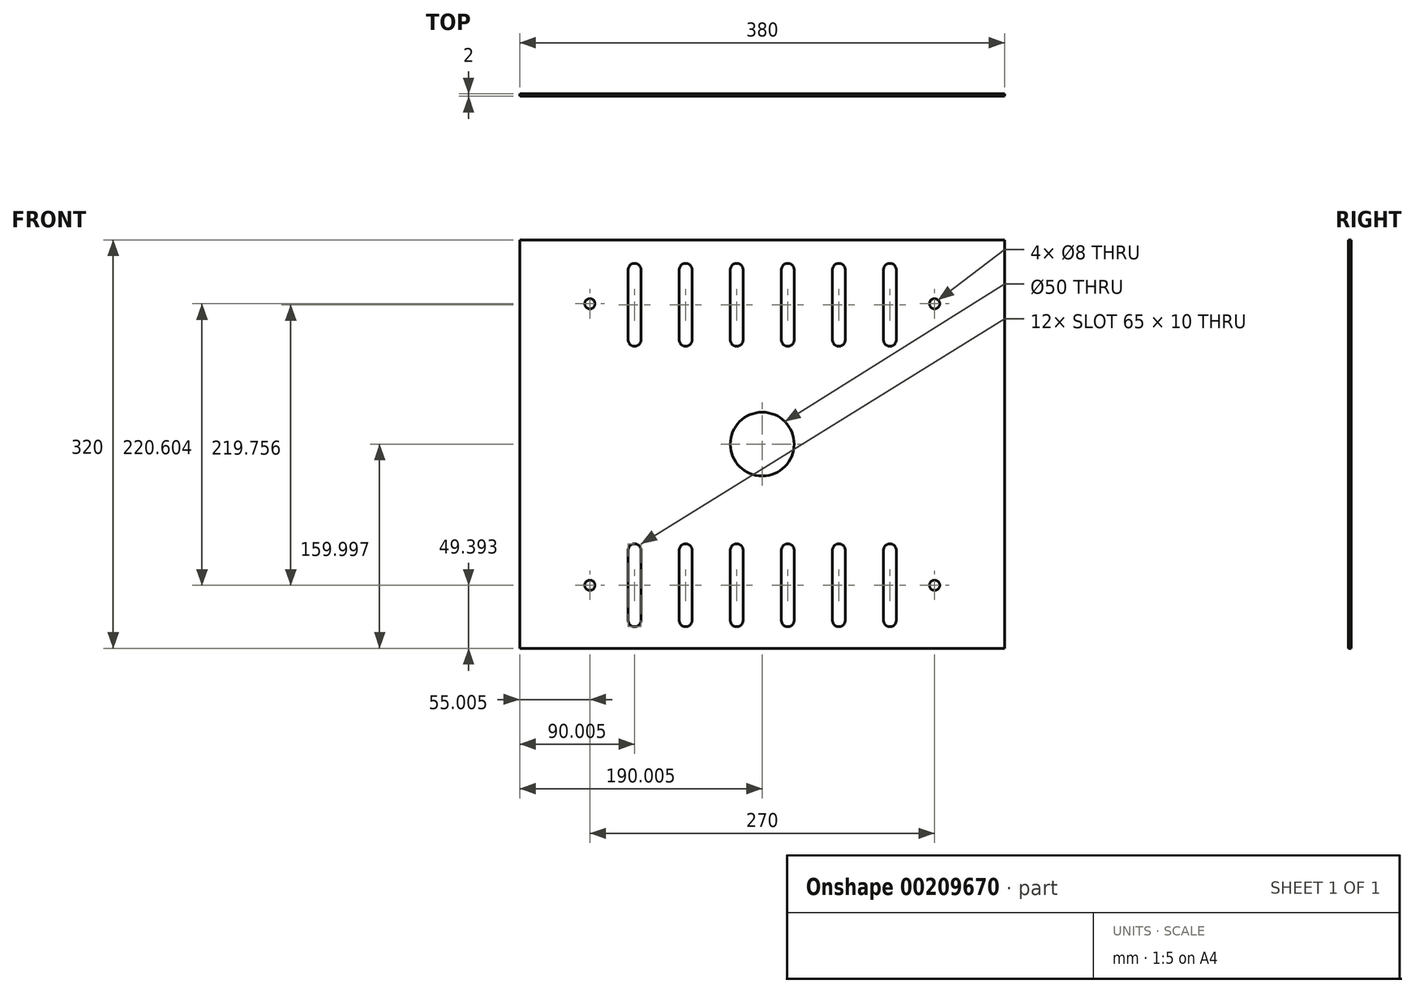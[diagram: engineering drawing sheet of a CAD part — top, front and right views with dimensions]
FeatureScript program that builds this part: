
annotation { "Feature Type Name" : "Feature", "Feature Type Description" : "" }
export const myFeature = defineFeature(function(context is Context, id is Id, definition is map)
    precondition{}
    {
        {
            var Q0;
            Q0=qCreatedBy(makeId("Front.planeOp"),FACE);
            var sketch = newSketch(context, id + "F0", { "sketchPlane" : qUnion([Q0])});
            skLineSegment(sketch, "E0.bottom", {"start": v(-8022.28, 365.36) * mm, "end": v(-7642.28, 365.36) * mm});
            skLineSegment(sketch, "E0.top", {"start": v(-8022.28, 45.36) * mm, "end": v(-7642.28, 45.36) * mm});
            skLineSegment(sketch, "E0.left", {"start": v(-8022.28, 365.36) * mm, "end": v(-8022.28, 45.36) * mm});
            skLineSegment(sketch, "E0.right", {"start": v(-7642.28, 365.36) * mm, "end": v(-7642.28, 45.36) * mm});
            skPoint(sketch, "E1", {"position": v(-7967.28, 315.36) * mm});
            skPoint(sketch, "E2", {"position": v(-7697.28, 315.36) * mm});
            skPoint(sketch, "E3", {"position": v(-7967.28, 94.75) * mm});
            skPoint(sketch, "E4", {"position": v(-7697.28, 94.75) * mm});
            skPoint(sketch, "E5", {"position": v(-7832.28, 365.36) * mm});
            skPoint(sketch, "E6", {"position": v(-8022.28, 205.36) * mm});
            skPoint(sketch, "E7", {"position": v(-7832.28, 205.36) * mm});
            skCircle(sketch, "E8", {"center": v(-7832.28, 205.36) * mm, "radius": 25 * mm});
            skCircle(sketch, "E9", {"center": v(-7967.28, 315.36) * mm, "radius": 4 * mm});
            skCircle(sketch, "E10", {"center": v(-7967.28, 94.75) * mm, "radius": 4 * mm});
            skCircle(sketch, "E11", {"center": v(-7697.28, 315.36) * mm, "radius": 4 * mm});
            skCircle(sketch, "E12", {"center": v(-7697.28, 94.75) * mm, "radius": 4 * mm});
            skPoint(sketch, "E13", {"position": v(-7932.28, 94.75) * mm});
            skLineSegment(sketch, "E14.bottom", {"start": v(-7932.28, 127.25) * mm, "end": v(-7932.28, 127.25) * mm});
            skLineSegment(sketch, "E14.top", {"start": v(-7932.28, 62.25) * mm, "end": v(-7932.28, 62.25) * mm});
            skLineSegment(sketch, "E14.left", {"start": v(-7927.28, 122.25) * mm, "end": v(-7927.28, 67.25) * mm});
            skLineSegment(sketch, "E14.right", {"start": v(-7937.28, 122.25) * mm, "end": v(-7937.28, 67.25) * mm});
            skPoint(sketch, "E15.visualSharp", {"position": v(-7937.28, 127.25) * mm});
            skArc(sketch, "E15.filletArc", {"start": v(-7932.28, 127.25) * mm, "mid": v(-7935.81, 125.79) * mm, "end": v(-7937.28, 122.25) * mm});
            skPoint(sketch, "E16.visualSharp", {"position": v(-7927.28, 127.25) * mm});
            skArc(sketch, "E16.filletArc", {"start": v(-7927.28, 122.25) * mm, "mid": v(-7928.74, 125.79) * mm, "end": v(-7932.28, 127.25) * mm});
            skPoint(sketch, "E17.visualSharp", {"position": v(-7927.28, 62.25) * mm});
            skArc(sketch, "E17.filletArc", {"start": v(-7932.28, 62.25) * mm, "mid": v(-7928.74, 63.72) * mm, "end": v(-7927.28, 67.25) * mm});
            skPoint(sketch, "E18.visualSharp", {"position": v(-7937.28, 62.25) * mm});
            skArc(sketch, "E18.filletArc", {"start": v(-7937.28, 67.25) * mm, "mid": v(-7935.81, 63.72) * mm, "end": v(-7932.28, 62.25) * mm});
            skPoint(sketch, "E19", {"position": v(-7892.28, 94.75) * mm});
            skLineSegment(sketch, "E20.bottom", {"start": v(-7892.28, 127.25) * mm, "end": v(-7892.28, 127.25) * mm});
            skLineSegment(sketch, "E20.top", {"start": v(-7892.28, 62.25) * mm, "end": v(-7892.28, 62.25) * mm});
            skLineSegment(sketch, "E20.left", {"start": v(-7887.28, 122.25) * mm, "end": v(-7887.28, 67.25) * mm});
            skLineSegment(sketch, "E20.right", {"start": v(-7897.28, 122.25) * mm, "end": v(-7897.28, 67.25) * mm});
            skPoint(sketch, "E21.visualSharp", {"position": v(-7897.28, 127.25) * mm});
            skArc(sketch, "E21.filletArc", {"start": v(-7892.28, 127.25) * mm, "mid": v(-7895.81, 125.79) * mm, "end": v(-7897.28, 122.25) * mm});
            skPoint(sketch, "E22.visualSharp", {"position": v(-7887.28, 127.25) * mm});
            skArc(sketch, "E22.filletArc", {"start": v(-7887.28, 122.25) * mm, "mid": v(-7888.74, 125.79) * mm, "end": v(-7892.28, 127.25) * mm});
            skPoint(sketch, "E23.visualSharp", {"position": v(-7887.28, 62.25) * mm});
            skArc(sketch, "E23.filletArc", {"start": v(-7892.28, 62.25) * mm, "mid": v(-7888.74, 63.72) * mm, "end": v(-7887.28, 67.25) * mm});
            skPoint(sketch, "E24.visualSharp", {"position": v(-7897.28, 62.25) * mm});
            skArc(sketch, "E24.filletArc", {"start": v(-7897.28, 67.25) * mm, "mid": v(-7895.81, 63.72) * mm, "end": v(-7892.28, 62.25) * mm});
            skPoint(sketch, "E25", {"position": v(-7852.28, 94.75) * mm});
            skLineSegment(sketch, "E26.bottom", {"start": v(-7852.28, 127.25) * mm, "end": v(-7852.28, 127.25) * mm});
            skLineSegment(sketch, "E26.top", {"start": v(-7852.28, 62.25) * mm, "end": v(-7852.28, 62.25) * mm});
            skLineSegment(sketch, "E26.left", {"start": v(-7847.28, 122.25) * mm, "end": v(-7847.28, 67.25) * mm});
            skLineSegment(sketch, "E26.right", {"start": v(-7857.28, 122.25) * mm, "end": v(-7857.28, 67.25) * mm});
            skPoint(sketch, "E27.visualSharp", {"position": v(-7857.28, 127.25) * mm});
            skArc(sketch, "E27.filletArc", {"start": v(-7852.28, 127.25) * mm, "mid": v(-7855.81, 125.79) * mm, "end": v(-7857.28, 122.25) * mm});
            skPoint(sketch, "E28.visualSharp", {"position": v(-7847.28, 127.25) * mm});
            skArc(sketch, "E28.filletArc", {"start": v(-7847.28, 122.25) * mm, "mid": v(-7848.74, 125.79) * mm, "end": v(-7852.28, 127.25) * mm});
            skPoint(sketch, "E29.visualSharp", {"position": v(-7847.28, 62.25) * mm});
            skArc(sketch, "E29.filletArc", {"start": v(-7852.28, 62.25) * mm, "mid": v(-7848.74, 63.72) * mm, "end": v(-7847.28, 67.25) * mm});
            skPoint(sketch, "E30.visualSharp", {"position": v(-7857.28, 62.25) * mm});
            skArc(sketch, "E30.filletArc", {"start": v(-7857.28, 67.25) * mm, "mid": v(-7855.81, 63.72) * mm, "end": v(-7852.28, 62.25) * mm});
            skPoint(sketch, "E31", {"position": v(-7812.28, 94.75) * mm});
            skLineSegment(sketch, "E32.bottom", {"start": v(-7812.28, 127.25) * mm, "end": v(-7812.28, 127.25) * mm});
            skLineSegment(sketch, "E32.top", {"start": v(-7812.28, 62.25) * mm, "end": v(-7812.28, 62.25) * mm});
            skLineSegment(sketch, "E32.left", {"start": v(-7807.28, 122.25) * mm, "end": v(-7807.28, 67.25) * mm});
            skLineSegment(sketch, "E32.right", {"start": v(-7817.28, 122.25) * mm, "end": v(-7817.28, 67.25) * mm});
            skPoint(sketch, "E33.visualSharp", {"position": v(-7817.28, 127.25) * mm});
            skArc(sketch, "E33.filletArc", {"start": v(-7812.28, 127.25) * mm, "mid": v(-7815.81, 125.79) * mm, "end": v(-7817.28, 122.25) * mm});
            skPoint(sketch, "E34.visualSharp", {"position": v(-7807.28, 127.25) * mm});
            skArc(sketch, "E34.filletArc", {"start": v(-7807.28, 122.25) * mm, "mid": v(-7808.74, 125.79) * mm, "end": v(-7812.28, 127.25) * mm});
            skPoint(sketch, "E35.visualSharp", {"position": v(-7807.28, 62.25) * mm});
            skArc(sketch, "E35.filletArc", {"start": v(-7812.28, 62.25) * mm, "mid": v(-7808.74, 63.72) * mm, "end": v(-7807.28, 67.25) * mm});
            skPoint(sketch, "E36.visualSharp", {"position": v(-7817.28, 62.25) * mm});
            skArc(sketch, "E36.filletArc", {"start": v(-7817.28, 67.25) * mm, "mid": v(-7815.81, 63.72) * mm, "end": v(-7812.28, 62.25) * mm});
            skPoint(sketch, "E37", {"position": v(-7772.28, 94.75) * mm});
            skLineSegment(sketch, "E38.bottom", {"start": v(-7772.28, 127.25) * mm, "end": v(-7772.28, 127.25) * mm});
            skLineSegment(sketch, "E38.top", {"start": v(-7772.28, 62.25) * mm, "end": v(-7772.28, 62.25) * mm});
            skLineSegment(sketch, "E38.left", {"start": v(-7767.28, 122.25) * mm, "end": v(-7767.28, 67.25) * mm});
            skLineSegment(sketch, "E38.right", {"start": v(-7777.28, 122.25) * mm, "end": v(-7777.28, 67.25) * mm});
            skPoint(sketch, "E39.visualSharp", {"position": v(-7777.28, 127.25) * mm});
            skArc(sketch, "E39.filletArc", {"start": v(-7772.28, 127.25) * mm, "mid": v(-7775.81, 125.79) * mm, "end": v(-7777.28, 122.25) * mm});
            skPoint(sketch, "E40.visualSharp", {"position": v(-7767.28, 127.25) * mm});
            skArc(sketch, "E40.filletArc", {"start": v(-7767.28, 122.25) * mm, "mid": v(-7768.74, 125.79) * mm, "end": v(-7772.28, 127.25) * mm});
            skPoint(sketch, "E41.visualSharp", {"position": v(-7767.28, 62.25) * mm});
            skArc(sketch, "E41.filletArc", {"start": v(-7772.28, 62.25) * mm, "mid": v(-7768.74, 63.72) * mm, "end": v(-7767.28, 67.25) * mm});
            skPoint(sketch, "E42.visualSharp", {"position": v(-7777.28, 62.25) * mm});
            skArc(sketch, "E42.filletArc", {"start": v(-7777.28, 67.25) * mm, "mid": v(-7775.81, 63.72) * mm, "end": v(-7772.28, 62.25) * mm});
            skPoint(sketch, "E43", {"position": v(-7732.28, 94.75) * mm});
            skLineSegment(sketch, "E44.bottom", {"start": v(-7732.28, 127.25) * mm, "end": v(-7732.28, 127.25) * mm});
            skLineSegment(sketch, "E44.top", {"start": v(-7732.28, 62.25) * mm, "end": v(-7732.28, 62.25) * mm});
            skLineSegment(sketch, "E44.left", {"start": v(-7727.28, 122.25) * mm, "end": v(-7727.28, 67.25) * mm});
            skLineSegment(sketch, "E44.right", {"start": v(-7737.28, 122.25) * mm, "end": v(-7737.28, 67.25) * mm});
            skPoint(sketch, "E45.visualSharp", {"position": v(-7737.28, 127.25) * mm});
            skArc(sketch, "E45.filletArc", {"start": v(-7732.28, 127.25) * mm, "mid": v(-7735.81, 125.79) * mm, "end": v(-7737.28, 122.25) * mm});
            skPoint(sketch, "E46.visualSharp", {"position": v(-7727.28, 127.25) * mm});
            skArc(sketch, "E46.filletArc", {"start": v(-7727.28, 122.25) * mm, "mid": v(-7728.74, 125.79) * mm, "end": v(-7732.28, 127.25) * mm});
            skPoint(sketch, "E47.visualSharp", {"position": v(-7727.28, 62.25) * mm});
            skArc(sketch, "E47.filletArc", {"start": v(-7732.28, 62.25) * mm, "mid": v(-7728.74, 63.72) * mm, "end": v(-7727.28, 67.25) * mm});
            skPoint(sketch, "E48.visualSharp", {"position": v(-7737.28, 62.25) * mm});
            skArc(sketch, "E48.filletArc", {"start": v(-7737.28, 67.25) * mm, "mid": v(-7735.81, 63.72) * mm, "end": v(-7732.28, 62.25) * mm});
            skPoint(sketch, "E49", {"position": v(-7932.28, 314.5) * mm});
            skLineSegment(sketch, "E50.bottom", {"start": v(-7932.28, 347) * mm, "end": v(-7932.28, 347) * mm});
            skLineSegment(sketch, "E50.top", {"start": v(-7932.28, 282) * mm, "end": v(-7932.28, 282) * mm});
            skLineSegment(sketch, "E50.left", {"start": v(-7927.28, 342) * mm, "end": v(-7927.28, 287) * mm});
            skLineSegment(sketch, "E50.right", {"start": v(-7937.28, 342) * mm, "end": v(-7937.28, 287) * mm});
            skPoint(sketch, "E51.visualSharp", {"position": v(-7937.28, 347) * mm});
            skArc(sketch, "E51.filletArc", {"start": v(-7932.28, 347) * mm, "mid": v(-7935.81, 345.54) * mm, "end": v(-7937.28, 342) * mm});
            skPoint(sketch, "E52.visualSharp", {"position": v(-7927.28, 347) * mm});
            skArc(sketch, "E52.filletArc", {"start": v(-7927.28, 342) * mm, "mid": v(-7928.74, 345.54) * mm, "end": v(-7932.28, 347) * mm});
            skPoint(sketch, "E53.visualSharp", {"position": v(-7927.28, 282) * mm});
            skArc(sketch, "E53.filletArc", {"start": v(-7932.28, 282) * mm, "mid": v(-7928.74, 283.47) * mm, "end": v(-7927.28, 287) * mm});
            skPoint(sketch, "E54.visualSharp", {"position": v(-7937.28, 282) * mm});
            skArc(sketch, "E54.filletArc", {"start": v(-7937.28, 287) * mm, "mid": v(-7935.81, 283.47) * mm, "end": v(-7932.28, 282) * mm});
            skPoint(sketch, "E55", {"position": v(-7892.28, 314.5) * mm});
            skLineSegment(sketch, "E56.bottom", {"start": v(-7892.28, 347) * mm, "end": v(-7892.28, 347) * mm});
            skLineSegment(sketch, "E56.top", {"start": v(-7892.28, 282) * mm, "end": v(-7892.28, 282) * mm});
            skLineSegment(sketch, "E56.left", {"start": v(-7887.28, 342) * mm, "end": v(-7887.28, 287) * mm});
            skLineSegment(sketch, "E56.right", {"start": v(-7897.28, 342) * mm, "end": v(-7897.28, 287) * mm});
            skPoint(sketch, "E57.visualSharp", {"position": v(-7897.28, 347) * mm});
            skArc(sketch, "E57.filletArc", {"start": v(-7892.28, 347) * mm, "mid": v(-7895.81, 345.54) * mm, "end": v(-7897.28, 342) * mm});
            skPoint(sketch, "E58.visualSharp", {"position": v(-7887.28, 347) * mm});
            skArc(sketch, "E58.filletArc", {"start": v(-7887.28, 342) * mm, "mid": v(-7888.74, 345.54) * mm, "end": v(-7892.28, 347) * mm});
            skPoint(sketch, "E59.visualSharp", {"position": v(-7887.28, 282) * mm});
            skArc(sketch, "E59.filletArc", {"start": v(-7892.28, 282) * mm, "mid": v(-7888.74, 283.47) * mm, "end": v(-7887.28, 287) * mm});
            skPoint(sketch, "E60.visualSharp", {"position": v(-7897.28, 282) * mm});
            skArc(sketch, "E60.filletArc", {"start": v(-7897.28, 287) * mm, "mid": v(-7895.81, 283.47) * mm, "end": v(-7892.28, 282) * mm});
            skPoint(sketch, "E61", {"position": v(-7852.28, 314.5) * mm});
            skLineSegment(sketch, "E62.bottom", {"start": v(-7852.28, 347) * mm, "end": v(-7852.28, 347) * mm});
            skLineSegment(sketch, "E62.top", {"start": v(-7852.28, 282) * mm, "end": v(-7852.28, 282) * mm});
            skLineSegment(sketch, "E62.left", {"start": v(-7847.28, 342) * mm, "end": v(-7847.28, 287) * mm});
            skLineSegment(sketch, "E62.right", {"start": v(-7857.28, 342) * mm, "end": v(-7857.28, 287) * mm});
            skPoint(sketch, "E63.visualSharp", {"position": v(-7857.28, 347) * mm});
            skArc(sketch, "E63.filletArc", {"start": v(-7852.28, 347) * mm, "mid": v(-7855.81, 345.54) * mm, "end": v(-7857.28, 342) * mm});
            skPoint(sketch, "E64.visualSharp", {"position": v(-7847.28, 347) * mm});
            skArc(sketch, "E64.filletArc", {"start": v(-7847.28, 342) * mm, "mid": v(-7848.74, 345.54) * mm, "end": v(-7852.28, 347) * mm});
            skPoint(sketch, "E65.visualSharp", {"position": v(-7847.28, 282) * mm});
            skArc(sketch, "E65.filletArc", {"start": v(-7852.28, 282) * mm, "mid": v(-7848.74, 283.47) * mm, "end": v(-7847.28, 287) * mm});
            skPoint(sketch, "E66.visualSharp", {"position": v(-7857.28, 282) * mm});
            skArc(sketch, "E66.filletArc", {"start": v(-7857.28, 287) * mm, "mid": v(-7855.81, 283.47) * mm, "end": v(-7852.28, 282) * mm});
            skPoint(sketch, "E67", {"position": v(-7812.28, 314.5) * mm});
            skLineSegment(sketch, "E68.bottom", {"start": v(-7812.28, 347) * mm, "end": v(-7812.28, 347) * mm});
            skLineSegment(sketch, "E68.top", {"start": v(-7812.28, 282) * mm, "end": v(-7812.28, 282) * mm});
            skLineSegment(sketch, "E68.left", {"start": v(-7807.28, 342) * mm, "end": v(-7807.28, 287) * mm});
            skLineSegment(sketch, "E68.right", {"start": v(-7817.28, 342) * mm, "end": v(-7817.28, 287) * mm});
            skPoint(sketch, "E69.visualSharp", {"position": v(-7817.28, 347) * mm});
            skArc(sketch, "E69.filletArc", {"start": v(-7812.28, 347) * mm, "mid": v(-7815.81, 345.54) * mm, "end": v(-7817.28, 342) * mm});
            skPoint(sketch, "E70.visualSharp", {"position": v(-7807.28, 347) * mm});
            skArc(sketch, "E70.filletArc", {"start": v(-7807.28, 342) * mm, "mid": v(-7808.74, 345.54) * mm, "end": v(-7812.28, 347) * mm});
            skPoint(sketch, "E71.visualSharp", {"position": v(-7807.28, 282) * mm});
            skArc(sketch, "E71.filletArc", {"start": v(-7812.28, 282) * mm, "mid": v(-7808.74, 283.47) * mm, "end": v(-7807.28, 287) * mm});
            skPoint(sketch, "E72.visualSharp", {"position": v(-7817.28, 282) * mm});
            skArc(sketch, "E72.filletArc", {"start": v(-7817.28, 287) * mm, "mid": v(-7815.81, 283.47) * mm, "end": v(-7812.28, 282) * mm});
            skPoint(sketch, "E73", {"position": v(-7772.28, 314.5) * mm});
            skLineSegment(sketch, "E74.bottom", {"start": v(-7772.28, 347) * mm, "end": v(-7772.28, 347) * mm});
            skLineSegment(sketch, "E74.top", {"start": v(-7772.28, 282) * mm, "end": v(-7772.28, 282) * mm});
            skLineSegment(sketch, "E74.left", {"start": v(-7767.28, 342) * mm, "end": v(-7767.28, 287) * mm});
            skLineSegment(sketch, "E74.right", {"start": v(-7777.28, 342) * mm, "end": v(-7777.28, 287) * mm});
            skPoint(sketch, "E75.visualSharp", {"position": v(-7777.28, 347) * mm});
            skArc(sketch, "E75.filletArc", {"start": v(-7772.28, 347) * mm, "mid": v(-7775.81, 345.54) * mm, "end": v(-7777.28, 342) * mm});
            skPoint(sketch, "E76.visualSharp", {"position": v(-7767.28, 347) * mm});
            skArc(sketch, "E76.filletArc", {"start": v(-7767.28, 342) * mm, "mid": v(-7768.74, 345.54) * mm, "end": v(-7772.28, 347) * mm});
            skPoint(sketch, "E77.visualSharp", {"position": v(-7767.28, 282) * mm});
            skArc(sketch, "E77.filletArc", {"start": v(-7772.28, 282) * mm, "mid": v(-7768.74, 283.47) * mm, "end": v(-7767.28, 287) * mm});
            skPoint(sketch, "E78.visualSharp", {"position": v(-7777.28, 282) * mm});
            skArc(sketch, "E78.filletArc", {"start": v(-7777.28, 287) * mm, "mid": v(-7775.81, 283.47) * mm, "end": v(-7772.28, 282) * mm});
            skPoint(sketch, "E79", {"position": v(-7732.28, 314.5) * mm});
            skLineSegment(sketch, "E80.bottom", {"start": v(-7732.28, 347) * mm, "end": v(-7732.28, 347) * mm});
            skLineSegment(sketch, "E80.top", {"start": v(-7732.28, 282) * mm, "end": v(-7732.28, 282) * mm});
            skLineSegment(sketch, "E80.left", {"start": v(-7727.28, 342) * mm, "end": v(-7727.28, 287) * mm});
            skLineSegment(sketch, "E80.right", {"start": v(-7737.28, 342) * mm, "end": v(-7737.28, 287) * mm});
            skPoint(sketch, "E81.visualSharp", {"position": v(-7737.28, 347) * mm});
            skArc(sketch, "E81.filletArc", {"start": v(-7732.28, 347) * mm, "mid": v(-7735.81, 345.54) * mm, "end": v(-7737.28, 342) * mm});
            skPoint(sketch, "E82.visualSharp", {"position": v(-7727.28, 347) * mm});
            skArc(sketch, "E82.filletArc", {"start": v(-7727.28, 342) * mm, "mid": v(-7728.74, 345.54) * mm, "end": v(-7732.28, 347) * mm});
            skPoint(sketch, "E83.visualSharp", {"position": v(-7727.28, 282) * mm});
            skArc(sketch, "E83.filletArc", {"start": v(-7732.28, 282) * mm, "mid": v(-7728.74, 283.47) * mm, "end": v(-7727.28, 287) * mm});
            skPoint(sketch, "E84.visualSharp", {"position": v(-7737.28, 282) * mm});
            skArc(sketch, "E84.filletArc", {"start": v(-7737.28, 287) * mm, "mid": v(-7735.81, 283.47) * mm, "end": v(-7732.28, 282) * mm});
            skSolve(sketch);
        }
        {
            var Q0;
            Q0=makeQuery(id+"F0.imprint","IMPRINT",FACE,{"disambiguationData":[TD([[makeQuery(id+"F0.imprint","IMPRINT",EDGE,{"derivedFrom":sQuery(id+"F0.wireOp",EDGE,"E0.bottom")}),-1.0]])]});
            extrude(context, id + "F1", {"entities" : qUnion([Q0]), "depth" : 2 * mm});
        }
    });
